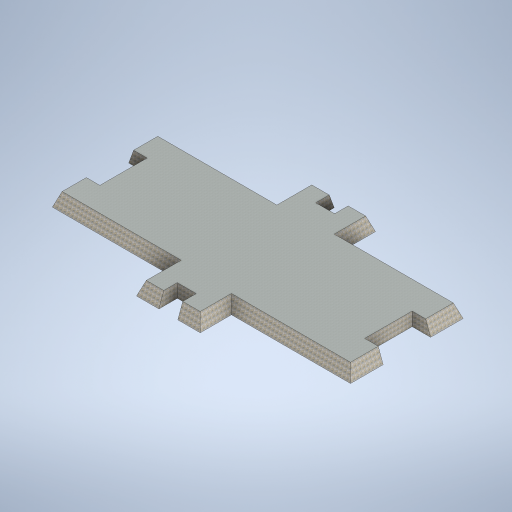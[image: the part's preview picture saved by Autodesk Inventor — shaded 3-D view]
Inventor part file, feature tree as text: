
AUTODESK INVENTOR PART (.ipt)
format: ipt  version: 2024.2 (Build 282272000, 272)  size: 358,912 bytes
history: native  units: mm
features: sketch x3, extrude x2
ambient origin geometry x8: Origin, YZ Plane, XZ Plane, XY Plane, X Axis, Y Axis, Z Axis, Center Point
bodies: Body1 (feature_tree)
feature tree (5):
  extrude  "Extrusion2"  Depth=3000.0mm
  extrude  "Extrusion3"  Depth=2000.0mm
  sketch  "Sketch3"  dims[d13=1400.0mm d14=2000.0mm d15=2800.0mm d16=1400.0mm d17=2000.0mm d18=2800.0mm d19=2000.0mm d21=3500.0mm d22=3500.0mm d23=2000.0mm d24=7000.0mm d25=2000.0mm d26=0.0mm d27=2000.0mm d28=7000.0mm d4=500.0mm d5=0.872665mm d6=500.0mm d7=0.872665mm]
  sketch  "Sketch1"  dims[d0=3000.0mm d1=3000.0mm]
  sketch  "Sketch2"  dims[d10=2000.0mm d11=3.490659mm d12=15200.0mm]
